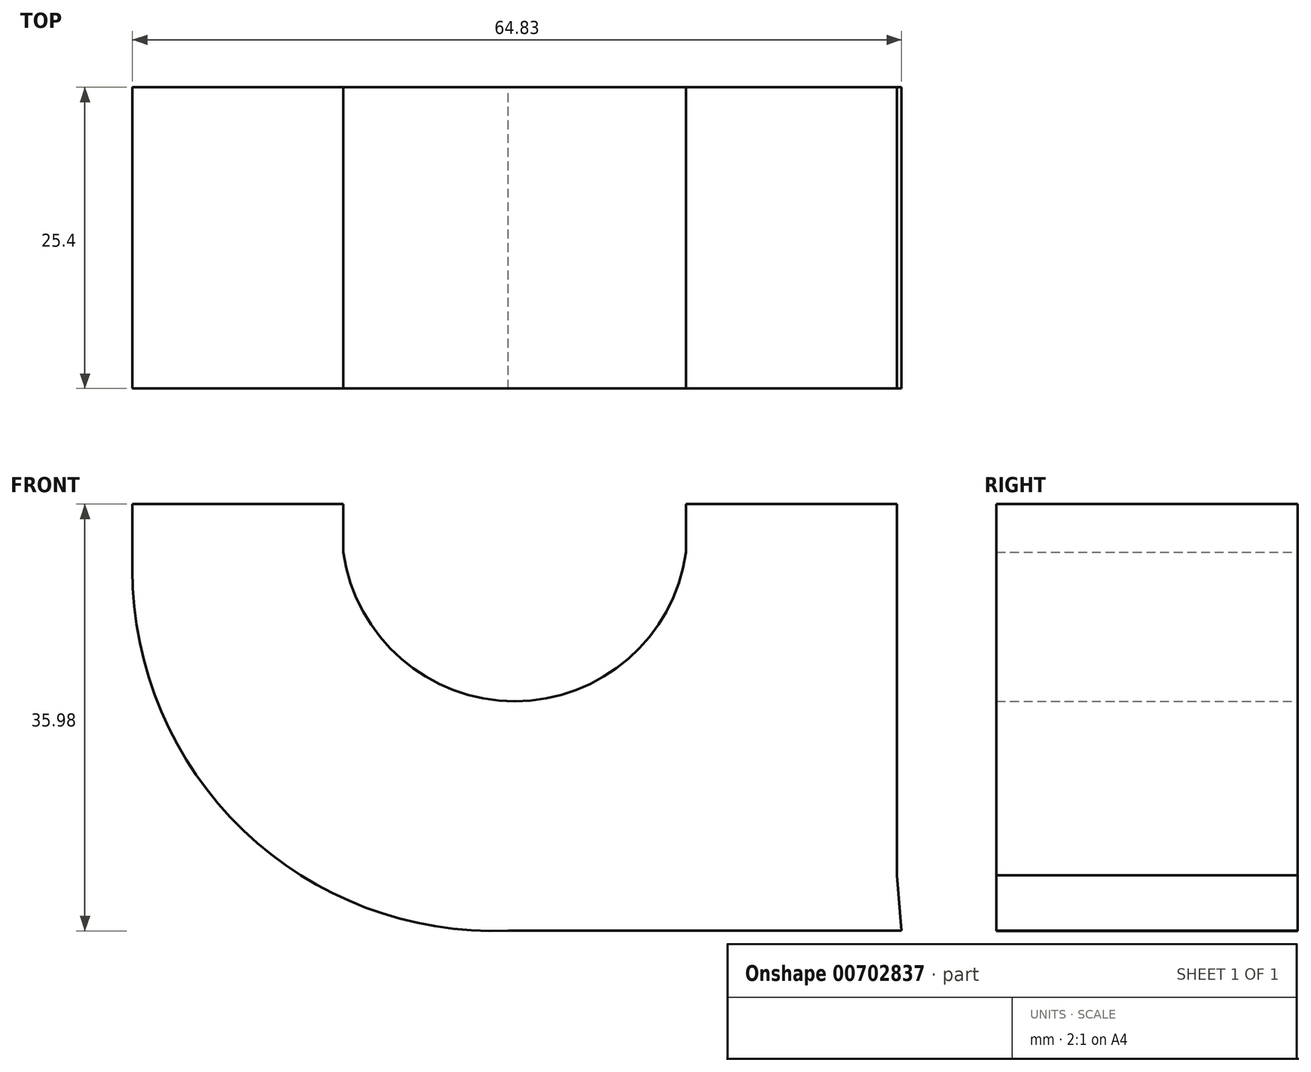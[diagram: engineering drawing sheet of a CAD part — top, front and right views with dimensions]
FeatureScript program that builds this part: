
annotation { "Feature Type Name" : "Feature", "Feature Type Description" : "" }
export const myFeature = defineFeature(function(context is Context, id is Id, definition is map)
    precondition{}
    {
        {
            var Q0;
            Q0=qCreatedBy(makeId("Front.planeOp"),FACE);
            var sketch = newSketch(context, id + "F0", { "sketchPlane" : qUnion([Q0])});
            skLineSegment(sketch, "E0.bottom", {"start": v(23.68, 13.36) * mm, "end": v(41.46, 13.36) * mm});
            skLineSegment(sketch, "E0.left", {"start": v(23.68, 13.36) * mm, "end": v(23.68, 9.3) * mm});
            skLineSegment(sketch, "E0.right", {"start": v(41.46, 13.36) * mm, "end": v(41.46, -17.93) * mm});
            skLineSegment(sketch, "E1.bottom", {"start": v(-23, 13.36) * mm, "end": v(-5.21, 13.36) * mm});
            skLineSegment(sketch, "E1.left", {"start": v(-23, 13.36) * mm, "end": v(-23, 7.8) * mm});
            skLineSegment(sketch, "E1.right", {"start": v(-5.21, 13.36) * mm, "end": v(-5.21, 7.8) * mm});
            skArc(sketch, "E2", {"start": v(-5.21, 13.36) * mm, "mid": v(9.23, -3.26) * mm, "end": v(23.68, 13.36) * mm});
            skArc(sketch, "E3", {"start": v(-23, 7.8) * mm, "mid": v(-13.64, -14.14) * mm, "end": v(8.67, -22.6) * mm});
            skLineSegment(sketch, "E4", {"start": v(8.67, -22.6) * mm, "end": v(41.84, -22.6) * mm});
            skLineSegment(sketch, "E5", {"start": v(41.84, -22.6) * mm, "end": v(41.46, -17.93) * mm});
            skSolve(sketch);
        }
        {
            var Q0;
            Q0 = qSketchRegion(id + "F0", true);
            extrude(context, id + "F1", {"entities" : qUnion([Q0]), "depth" : 25.4 * mm, "offsetDistance" : 25.4 * mm});
        }
    });
